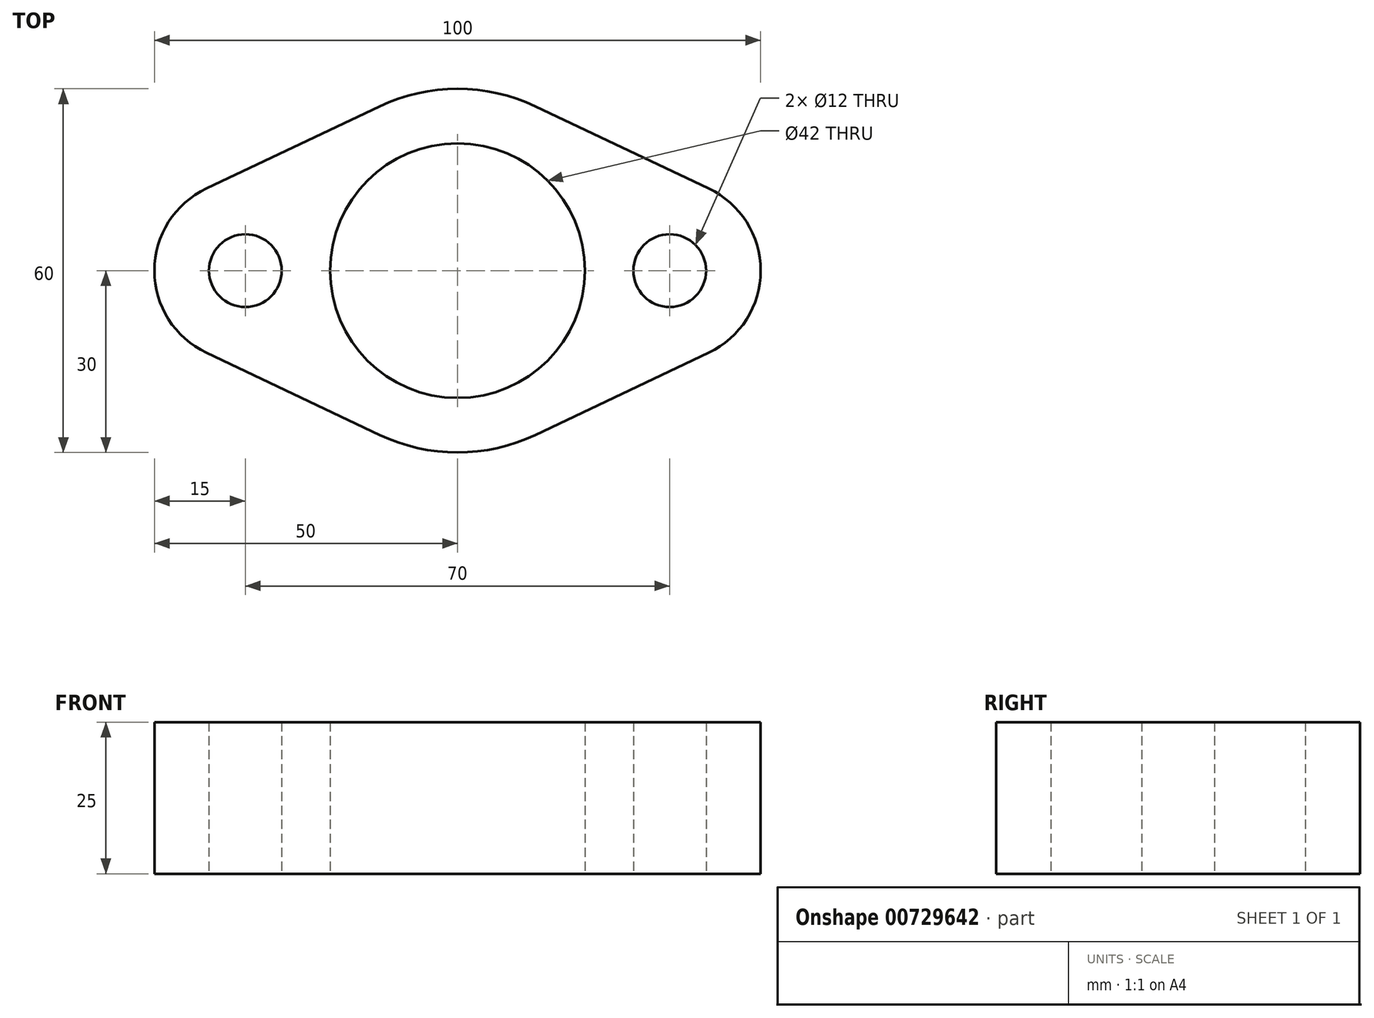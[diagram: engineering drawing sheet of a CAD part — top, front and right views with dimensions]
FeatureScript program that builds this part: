
annotation { "Feature Type Name" : "Feature", "Feature Type Description" : "" }
export const myFeature = defineFeature(function(context is Context, id is Id, definition is map)
    precondition{}
    {
        {
            var Q0;
            Q0=qCreatedBy(makeId("Top.planeOp"),FACE);
            var sketch = newSketch(context, id + "F0", { "sketchPlane" : qUnion([Q0])});
            skArc(sketch, "E0", {"start": v(0, -21) * mm, "mid": v(21, 0) * mm, "end": v(0, 21) * mm});
            skCircle(sketch, "E1", {"center": v(35, 0) * mm, "radius": 6 * mm});
            skLineSegment(sketch, "E2", {"start": v(12.86, 27.1) * mm, "end": v(41.43, 13.55) * mm});
            skLineSegment(sketch, "E3", {"start": v(12.86, -27.1) * mm, "end": v(41.43, -13.55) * mm});
            skArc(sketch, "E4.trimOffspring", {"start": v(0, -30) * mm, "mid": v(6.59, -29.27) * mm, "end": v(12.86, -27.1) * mm});
            skArc(sketch, "E5.trimOffspring", {"start": v(12.86, 27.1) * mm, "mid": v(6.59, 29.27) * mm, "end": v(0, 30) * mm});
            skArc(sketch, "E6.trimOffspring", {"start": v(41.43, -13.55) * mm, "mid": v(50, 0) * mm, "end": v(41.43, 13.55) * mm});
            skLineSegment(sketch, "E7", {"start": v(0, 63.31) * mm, "end": v(0, -61.05) * mm});
            skArc(sketch, "E8.MirrorCS", {"start": v(-12.86, 27.1) * mm, "mid": v(-6.59, 29.27) * mm, "end": v(0, 30) * mm});
            skArc(sketch, "E9.MirrorCS", {"start": v(0, -30) * mm, "mid": v(-6.59, -29.27) * mm, "end": v(-12.86, -27.1) * mm});
            skLineSegment(sketch, "E10.MirrorCS", {"start": v(-12.86, -27.1) * mm, "end": v(-41.43, -13.55) * mm});
            skLineSegment(sketch, "E11.MirrorCS", {"start": v(-12.86, 27.1) * mm, "end": v(-41.43, 13.55) * mm});
            skCircle(sketch, "E12.MirrorC", {"center": v(-35, 0) * mm, "radius": 6 * mm});
            skArc(sketch, "E13.MirrorCS", {"start": v(0, -21) * mm, "mid": v(-21, 0) * mm, "end": v(0, 21) * mm});
            skArc(sketch, "E14.MirrorCS", {"start": v(-41.43, -13.55) * mm, "mid": v(-50, 0) * mm, "end": v(-41.43, 13.55) * mm});
            skSolve(sketch);
        }
        {
            var Q0;
            Q0 = qSketchRegion(id + "F0", true);
            extrude(context, id + "F1", {"entities" : qUnion([Q0]), "depth" : 10 * mm, "offsetDistance" : 25 * mm});
        }
        {
            var Q0;
            Q0 = qSketchRegion(id + "F0", true);
            extrude(context, id + "F2", {"entities" : qUnion([Q0]), "operationType" : NewBodyOperationType.ADD, "depth" : 25 * mm, "offsetDistance" : 25 * mm});
        }
    });
